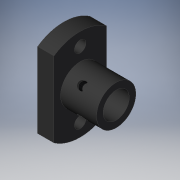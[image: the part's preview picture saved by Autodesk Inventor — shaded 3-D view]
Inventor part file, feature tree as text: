
AUTODESK INVENTOR PART (.ipt)
format: ipt  version: 2019 (Build 230136000, 136)  size: 173,568 bytes
history: native  units: mm
features: other x14, sketch x6, revolve x3, thread x2, hole x2, extrude x1
ambient origin geometry x8: Origin, YZ Plane, XZ Plane, XY Plane, X Axis, Y Axis, Z Axis, Center Point
bodies: Solid1 (feature_tree)
feature tree (28):
  revolve  "Revolution1"  Angle=360.0deg
  revolve  "Revolution2"  Angle=360.0deg
  thread  "Thread1"  [1 undecoded]
  revolve  "Revolution3"  [1 undecoded]
  thread  "Thread2"  [1 undecoded]
  hole  "Hole1"  [1 undecoded]
  hole  "Hole2"  [1 undecoded]
  extrude  "Extrusion1"  [1 undecoded]
  other  "to_screw1_XY"
  other  "to_screw1_YZ"
  other  "to_screw1_ZX"
  other  "to_screw1_X"
  other  "to_screw1_Y"
  other  "to_screw1_Z"
  other  "to_screw1_Center"
  other  "to_screw2_XY"
  other  "to_screw2_YZ"
  other  "to_screw2_ZX"
  other  "to_screw2_X"
  other  "to_screw2_Y"
  other  "to_screw2_Z"
  other  "to_screw2_Center"
  sketch  "Sketch_1"  dims[d0=360.0deg d1=360.0deg]
  sketch  "Sketch_19"
  sketch  "Sketch_3"  dims[d2=2.7295mm d3=0.0mm d4=360.0deg d5=2.7295mm d6=0.0mm]
  sketch  "Sketch4"  dims[d7=3.5mm d8=6.0mm d9=4.0mm d10=2.0mm d11=90.0deg d12=5.0mm d13=0.0mm]
  sketch  "Sketch5"
  sketch  "Sketch_4"  dims[d14=3.5mm d15=6.0mm d16=4.0mm d17=2.0mm d18=90.0deg d19=5.0mm d20=0.0mm d21=16.0mm d22=0.0mm]
note: 6 required parameter values undecoded (feature->parameter linkage not recoverable at this tier; creation-order binding heuristic only, values carry confidence <= 0.55)